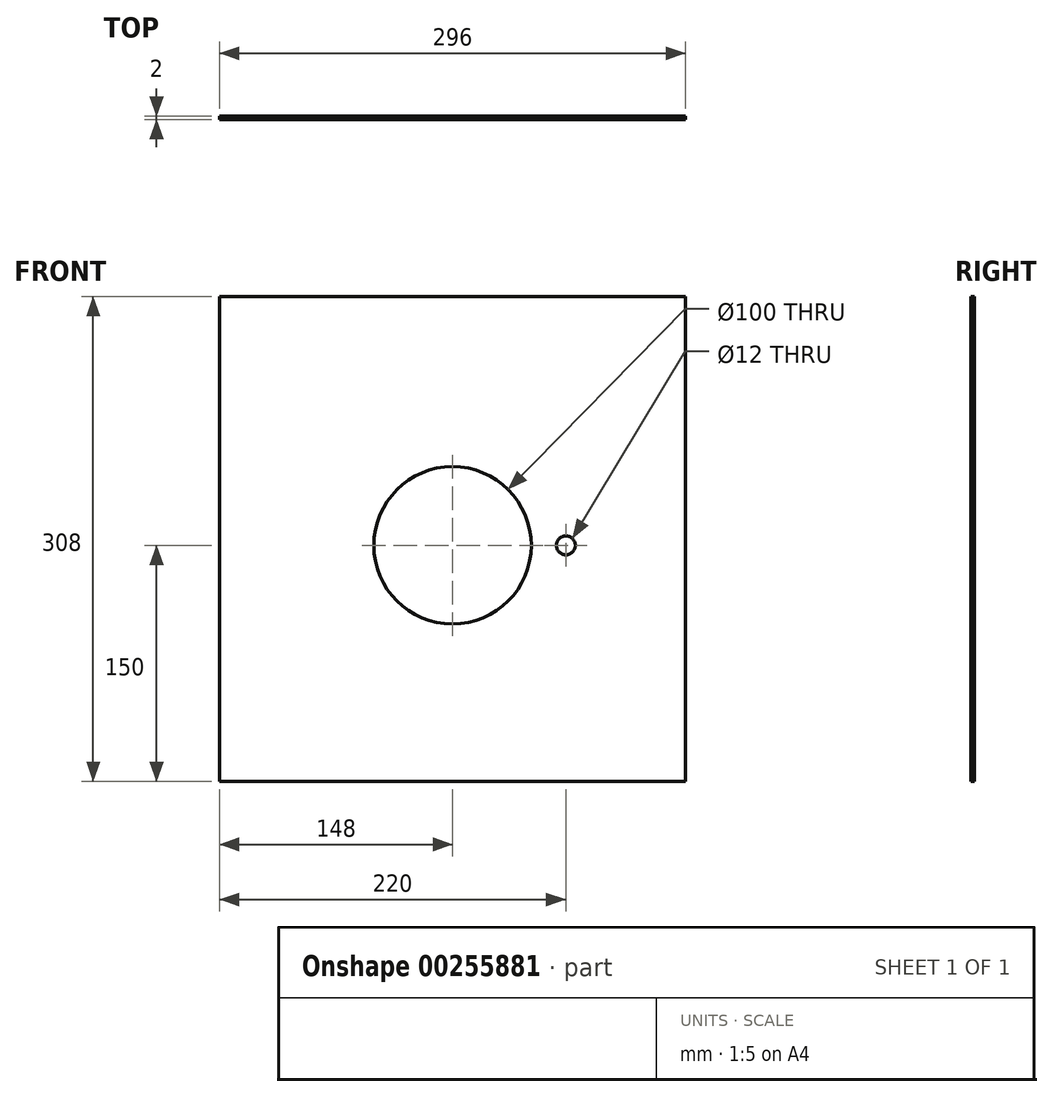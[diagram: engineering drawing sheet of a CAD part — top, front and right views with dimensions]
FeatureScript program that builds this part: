
annotation { "Feature Type Name" : "Feature", "Feature Type Description" : "" }
export const myFeature = defineFeature(function(context is Context, id is Id, definition is map)
    precondition{}
    {
        {
            var Q0;
            Q0=qCreatedBy(makeId("Front.planeOp"),FACE);
            var sketch = newSketch(context, id + "F0", { "sketchPlane" : qUnion([Q0])});
            skLineSegment(sketch, "E0.bottom", {"start": v(146, 153) * mm, "end": v(-150, 153) * mm});
            skLineSegment(sketch, "E0.top", {"start": v(146, -155) * mm, "end": v(-150, -155) * mm});
            skLineSegment(sketch, "E0.left", {"start": v(146, 153) * mm, "end": v(146, -155) * mm});
            skLineSegment(sketch, "E0.right", {"start": v(-150, 153) * mm, "end": v(-150, -155) * mm});
            skLineSegment(sketch, "E1", {"start": v(-2, 153) * mm, "end": v(-2, -155) * mm, "construction": true});
            skLineSegment(sketch, "E2", {"start": v(-150, 145) * mm, "end": v(146, 145) * mm, "construction": true});
            skLineSegment(sketch, "E3", {"start": v(-150, -5) * mm, "end": v(146, -5) * mm, "construction": true});
            skCircle(sketch, "E4", {"center": v(-2, -5) * mm, "radius": 50 * mm});
            skPoint(sketch, "E5", {"position": v(70, -5) * mm});
            skSolve(sketch);
        }
        {
            var Q0;
            Q0=makeQuery(id+"F0.imprint","IMPRINT",FACE,{"disambiguationData":[TD([[makeQuery(id+"F0.imprint","IMPRINT",EDGE,{"derivedFrom":sQuery(id+"F0.wireOp",EDGE,"E0.bottom")}),1.0]])]});
            extrude(context, id + "F1", {"entities" : qUnion([Q0]), "depth" : 2 * mm});
        }
        {
            var Q0;
            Q0=sQuery(id+"F0.wireOp",VERTEX,"E5");
            var Q1;
            Q1=makeQuery(id+"F1.opExtrude","SWEPT_BODY",BODY,{"disambiguationData":[OSD([sQuery(id+"F0.wireOp",EDGE,"E0.bottom"),sQuery(id+"F0.wireOp",EDGE,"E0.top"),sQuery(id+"F0.wireOp",EDGE,"E0.left"),sQuery(id+"F0.wireOp",EDGE,"E0.right"),sQuery(id+"F0.wireOp",EDGE,"E4")])]});
            hole(context, id + "F2", {"style" : HoleStyle.SIMPLE, "endStyle" : HoleEndStyle.THROUGH, "oppositeDirection" : true, "holeDiameter" : 12 * mm, "tappedDepth" : 12 * mm, "tapClearance" : 3, "locations" : qUnion([Q0]), "scope" : qUnion([Q1])});
        }
    });
